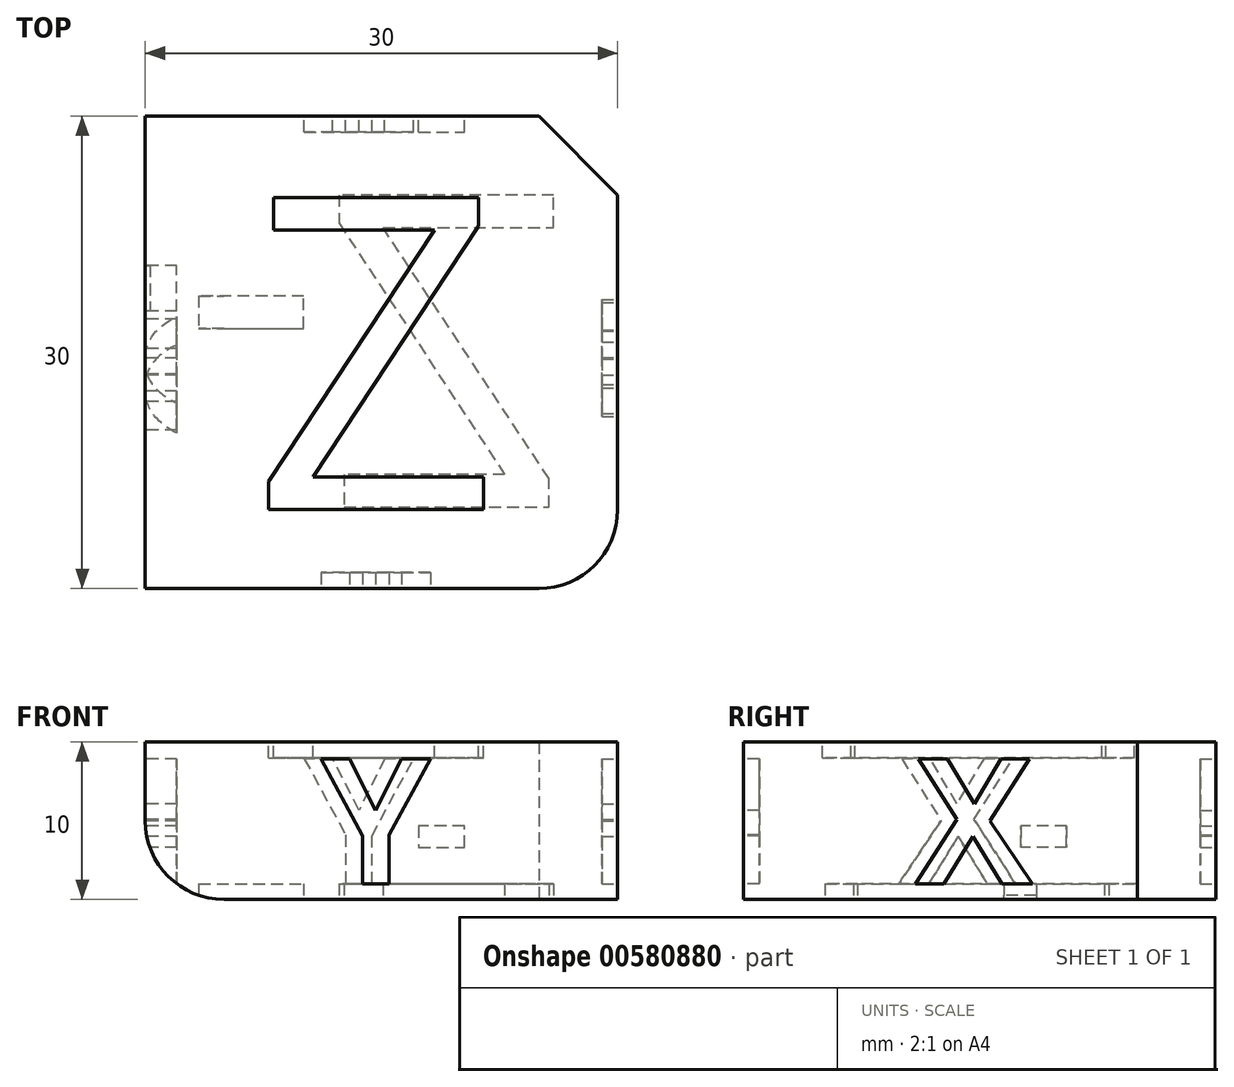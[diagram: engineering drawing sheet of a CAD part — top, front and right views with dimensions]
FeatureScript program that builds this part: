
annotation { "Feature Type Name" : "Feature", "Feature Type Description" : "" }
export const myFeature = defineFeature(function(context is Context, id is Id, definition is map)
    precondition{}
    {
        {
            var Q0;
            Q0=qCreatedBy(makeId("Top.planeOp"),FACE);
            var sketch = newSketch(context, id + "F0", { "sketchPlane" : qUnion([Q0])});
            skLineSegment(sketch, "E0.bottom", {"start": v(15, 15) * mm, "end": v(-15, 15) * mm});
            skLineSegment(sketch, "E0.top", {"start": v(15, -15) * mm, "end": v(-15, -15) * mm});
            skLineSegment(sketch, "E0.left", {"start": v(15, 15) * mm, "end": v(15, -15) * mm});
            skLineSegment(sketch, "E0.right", {"start": v(-15, 15) * mm, "end": v(-15, -15) * mm});
            skPoint(sketch, "E0.middle", {"position": v(0, 0) * mm});
            skSolve(sketch);
        }
        {
            var Q0;
            Q0=makeQuery(id+"F0.imprint","IMPRINT",FACE,{"disambiguationData":[TD([[makeQuery(id+"F0.imprint","IMPRINT",EDGE,{"derivedFrom":sQuery(id+"F0.wireOp",EDGE,"E0.bottom")}),1.0]])]});
            extrude(context, id + "F1", {"entities" : qUnion([Q0]), "depth" : 10 * mm, "offsetDistance" : 25 * mm});
        }
        {
            var Q0;
            Q0=makeQuery(id+"F1.opExtrude","SWEPT_EDGE",EDGE,{"disambiguationData":[OSD([sQuery(id+"F0.wireOp",EDGE,"E0.top"),sQuery(id+"F0.wireOp",EDGE,"E0.left")])]});
            fillet(context, id + "F2", {"entities" : qUnion([Q0]), "radius" : 5 * mm, "tangentPropagation" : true, "allowEdgeOverflow" : false});
        }
        {
            var Q0;
            Q0=makeQuery(id+"F1.opExtrude","SWEPT_EDGE",EDGE,{"disambiguationData":[OSD([sQuery(id+"F0.wireOp",EDGE,"E0.bottom"),sQuery(id+"F0.wireOp",EDGE,"E0.left")])]});
            chamfer(context, id + "F3", {"entities" : qUnion([Q0]), "width" : 5 * mm, "tangentPropagation" : true});
        }
        {
            var Q0;
            Q0=makeQuery(id+"F1.opExtrude","CAP_EDGE",EDGE,{"disambiguationData":[OSD([sQuery(id+"F0.wireOp",EDGE,"E0.right")])],"isStart":true});
            fillet(context, id + "F4", {"entities" : qUnion([Q0]), "radius" : 5 * mm, "tangentPropagation" : true, "allowEdgeOverflow" : false});
        }
        {
            var Q0;
            Q0=makeQuery(id+"F1.opExtrude","SWEPT_FACE",FACE,{"disambiguationData":[OSD([sQuery(id+"F0.wireOp",EDGE,"E0.top")])]});
            var sketch = newSketch(context, id + "F5", { "sketchPlane" : qUnion([Q0])});
            skText(sketch, "E1", { "text": "Y", "fontName": "OpenSans-Bold.ttf"});
            const initialGuessF5  = {"E1": [-0.00383, 0.001, 1, 0, 0.008]};
            skSetInitialGuess(sketch, initialGuessF5);
            skSolve(sketch);
        }
        {
            var Q0;
            Q0=makeQuery(id+"F5.imprint","IMPRINT",FACE,{"disambiguationData":[TD([[makeQuery(id+"F5.imprint","IMPRINT",EDGE,{"derivedFrom":sQuery(id+"F5.wireOp",EDGE,"E1.sketch_text.stroke-0")}),-1.0]])]});
            extrude(context, id + "F6", {"entities" : qUnion([Q0]), "operationType" : NewBodyOperationType.REMOVE, "oppositeDirection" : true, "depth" : 1 * mm, "offsetDistance" : 25 * mm});
        }
        {
            var Q0;
            Q0=makeQuery(id+"F1.opExtrude","SWEPT_FACE",FACE,{"disambiguationData":[OSD([sQuery(id+"F0.wireOp",EDGE,"E0.left")])]});
            var sketch = newSketch(context, id + "F7", { "sketchPlane" : qUnion([Q0])});
            skText(sketch, "E2", { "text": "X", "fontName": "OpenSans-Bold.ttf"});
            const initialGuessF7  = {"E2": [-0.00407, 0.001, 1, 0, 0.008]};
            skSetInitialGuess(sketch, initialGuessF7);
            skSolve(sketch);
        }
        {
            var Q0;
            Q0=makeQuery(id+"F7.imprint","IMPRINT",FACE,{"disambiguationData":[TD([[makeQuery(id+"F7.imprint","IMPRINT",EDGE,{"derivedFrom":sQuery(id+"F7.wireOp",EDGE,"E2.sketch_text.stroke-0")}),-1.0]])]});
            extrude(context, id + "F8", {"entities" : qUnion([Q0]), "operationType" : NewBodyOperationType.REMOVE, "oppositeDirection" : true, "depth" : 1 * mm, "offsetDistance" : 25 * mm});
        }
        {
            var Q0;
            Q0=makeQuery(id+"F1.opExtrude","SWEPT_FACE",FACE,{"disambiguationData":[OSD([sQuery(id+"F0.wireOp",EDGE,"E0.bottom")])]});
            var sketch = newSketch(context, id + "F9", { "sketchPlane" : qUnion([Q0])});
            skText(sketch, "E3", { "text": "-Y", "fontName": "OpenSans-Bold.ttf"});
            const initialGuessF9  = {"E3": [-0.00561, 0.001, 1, 0, 0.008]};
            skSetInitialGuess(sketch, initialGuessF9);
            skSolve(sketch);
        }
        {
            var Q0;
            Q0=makeQuery(id+"F9.imprint","IMPRINT",FACE,{"disambiguationData":[TD([[makeQuery(id+"F9.imprint","IMPRINT",EDGE,{"derivedFrom":sQuery(id+"F9.wireOp",EDGE,"E3.sketch_text.stroke-4")}),-1.0]])]});
            var Q1;
            Q1=makeQuery(id+"F9.imprint","IMPRINT",FACE,{"disambiguationData":[TD([[makeQuery(id+"F9.imprint","IMPRINT",EDGE,{"derivedFrom":sQuery(id+"F9.wireOp",EDGE,"E3.sketch_text.stroke-0")}),-1.0]])]});
            extrude(context, id + "F10", {"entities" : qUnion([Q0, Q1]), "operationType" : NewBodyOperationType.REMOVE, "oppositeDirection" : true, "depth" : 1 * mm, "offsetDistance" : 25 * mm});
        }
        {
            var Q0;
            Q0=makeQuery(id+"F1.opExtrude","SWEPT_FACE",FACE,{"disambiguationData":[OSD([sQuery(id+"F0.wireOp",EDGE,"E0.right")])]});
            var sketch = newSketch(context, id + "F11", { "sketchPlane" : qUnion([Q0])});
            skText(sketch, "E4", { "text": "-X", "fontName": "OpenSans-Bold.ttf"});
            const initialGuessF11  = {"E4": [-0.00585, 0.001, 1, 0, 0.008]};
            skSetInitialGuess(sketch, initialGuessF11);
            skSolve(sketch);
        }
        {
            var Q0;
            {var subQ6=sQuery(id+"F11.wireOp",EDGE,"E4.sketch_text.stroke-9");Q0=makeQuery(id+"F11.imprint","IMPRINT",FACE,{"disambiguationData":[TD([[makeQuery(id+"F11.imprint","IMPRINT",EDGE,{"derivedFrom":subQ6}),-1.0]])]});}
            var Q1;
            Q1=makeQuery(id+"F11.imprint","IMPRINT",FACE,{"disambiguationData":[TD([[makeQuery(id+"F11.imprint","IMPRINT",EDGE,{"derivedFrom":sQuery(id+"F11.wireOp",EDGE,"E4.sketch_text.stroke-4")}),-1.0]])]});
            var Q2;
            Q2=makeQuery(id+"F11.imprint","IMPRINT",FACE,{"disambiguationData":[TD([[makeQuery(id+"F11.imprint","IMPRINT",EDGE,{"derivedFrom":sQuery(id+"F11.wireOp",EDGE,"E4.sketch_text.stroke-0")}),-1.0]])]});
            extrude(context, id + "F12", {"entities" : qUnion([Q0, Q1, Q2]), "operationType" : NewBodyOperationType.REMOVE, "oppositeDirection" : true, "depth" : 2 * mm, "offsetDistance" : 25 * mm});
        }
        {
            var Q0;
            Q0=makeQuery(id+"F1.opExtrude","CAP_FACE",FACE,{"disambiguationData":[OSD([sQuery(id+"F0.wireOp",EDGE,"E0.bottom"),sQuery(id+"F0.wireOp",EDGE,"E0.top"),sQuery(id+"F0.wireOp",EDGE,"E0.left"),sQuery(id+"F0.wireOp",EDGE,"E0.right")])],"isStart":true});
            var sketch = newSketch(context, id + "F13", { "sketchPlane" : qUnion([Q0])});
            skText(sketch, "E5", { "text": "-Z", "fontName": "OpenSans-Regular.ttf"});
            const initialGuessF13  = {"E5": [-0.01274, -0.01, 1, 0, 0.02]};
            skSetInitialGuess(sketch, initialGuessF13);
            skSolve(sketch);
        }
        {
            var Q0;
            Q0=makeQuery(id+"F13.imprint","IMPRINT",FACE,{"disambiguationData":[TD([[makeQuery(id+"F13.imprint","IMPRINT",EDGE,{"derivedFrom":sQuery(id+"F13.wireOp",EDGE,"E5.sketch_text.stroke-4")}),-1.0]])]});
            var Q1;
            {var subQ0=sQuery(id+"F13.wireOp",EDGE,"E5.sketch_text.stroke-2");Q1=makeQuery(id+"F13.imprint","IMPRINT",FACE,{"disambiguationData":[TD([[makeQuery(id+"F13.imprint","IMPRINT",EDGE,{"derivedFrom":subQ0}),-1.0]])]});}
            var Q2;
            {var subQ0=sQuery(id+"F13.wireOp",EDGE,"E5.sketch_text.stroke-0");Q2=makeQuery(id+"F13.imprint","IMPRINT",FACE,{"disambiguationData":[TD([[makeQuery(id+"F13.imprint","IMPRINT",EDGE,{"derivedFrom":subQ0}),-1.0]])]});}
            extrude(context, id + "F14", {"entities" : qUnion([Q0, Q1, Q2]), "operationType" : NewBodyOperationType.REMOVE, "oppositeDirection" : true, "depth" : 1 * mm, "offsetDistance" : 25 * mm});
        }
        {
            var Q0;
            Q0=makeQuery(id+"F1.opExtrude","CAP_FACE",FACE,{"disambiguationData":[OSD([sQuery(id+"F0.wireOp",EDGE,"E0.bottom"),sQuery(id+"F0.wireOp",EDGE,"E0.top"),sQuery(id+"F0.wireOp",EDGE,"E0.left"),sQuery(id+"F0.wireOp",EDGE,"E0.right")])],"isStart":false});
            var sketch = newSketch(context, id + "F15", { "sketchPlane" : qUnion([Q0])});
            skText(sketch, "E6", { "text": "Z", "fontName": "OpenSans-Regular.ttf"});
            const initialGuessF15  = {"E6": [-0.00827, -0.01, 1, 0, 0.02]};
            skSetInitialGuess(sketch, initialGuessF15);
            skSolve(sketch);
        }
        {
            var Q0;
            Q0=makeQuery(id+"F15.imprint","IMPRINT",FACE,{"disambiguationData":[TD([[makeQuery(id+"F15.imprint","IMPRINT",EDGE,{"derivedFrom":sQuery(id+"F15.wireOp",EDGE,"E6.sketch_text.stroke-0")}),-1.0]])]});
            extrude(context, id + "F16", {"entities" : qUnion([Q0]), "operationType" : NewBodyOperationType.REMOVE, "oppositeDirection" : true, "depth" : 1 * mm, "offsetDistance" : 25 * mm});
        }
    });
